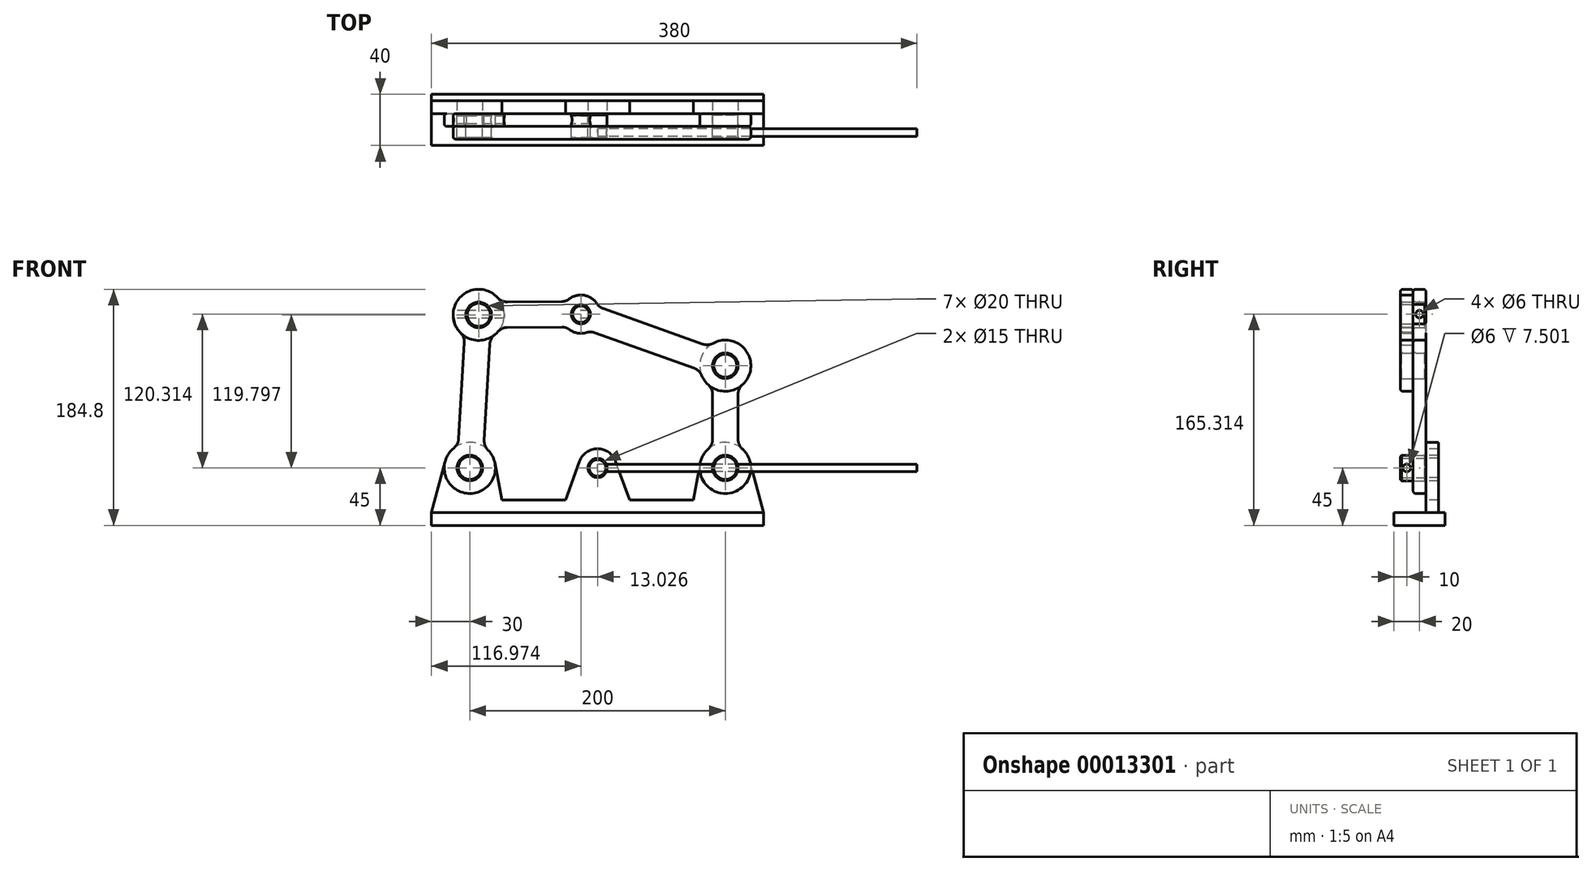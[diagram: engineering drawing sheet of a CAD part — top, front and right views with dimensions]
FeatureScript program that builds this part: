
annotation { "Feature Type Name" : "Feature", "Feature Type Description" : "" }
export const myFeature = defineFeature(function(context is Context, id is Id, definition is map)
    precondition{}
    {
        {
            var Q0;
            Q0=qCreatedBy(makeId("Front.planeOp"),FACE);
            var sketch = newSketch(context, id + "F0", { "sketchPlane" : qUnion([Q0])});
            skCircle(sketch, "E0", {"center": v(-93.03, 119.8) * mm, "radius": 20 * mm});
            skCircle(sketch, "E1", {"center": v(-93.03, 119.8) * mm, "radius": 10 * mm});
            skCircle(sketch, "E2", {"center": v(100, 80) * mm, "radius": 10 * mm});
            skCircle(sketch, "E3", {"center": v(100, 80) * mm, "radius": 20 * mm});
            skCircle(sketch, "E4", {"center": v(100, 0) * mm, "radius": 10 * mm});
            skCircle(sketch, "E5", {"center": v(100, 0) * mm, "radius": 20 * mm});
            skCircle(sketch, "E6", {"center": v(-100, 0) * mm, "radius": 10 * mm});
            skCircle(sketch, "E7", {"center": v(-100, 0) * mm, "radius": 20 * mm});
            skCircle(sketch, "E8", {"center": v(-13.03, 120.31) * mm, "radius": 7.5 * mm});
            skCircle(sketch, "E9", {"center": v(-13.03, 120.31) * mm, "radius": 15 * mm});
            skLineSegment(sketch, "E10", {"start": v(-75.77, 129.9) * mm, "end": v(-24.27, 130.24) * mm});
            skLineSegment(sketch, "E11", {"start": v(-75.64, 109.9) * mm, "end": v(-24.14, 110.24) * mm});
            skLineSegment(sketch, "E12", {"start": v(-5.85, 107.14) * mm, "end": v(80.33, 76.4) * mm});
            skLineSegment(sketch, "E13", {"start": v(90, 62.68) * mm, "end": v(90, 17.32) * mm});
            skLineSegment(sketch, "E14", {"start": v(110, 62.68) * mm, "end": v(110, 17.32) * mm});
            skLineSegment(sketch, "E15", {"start": v(-104.02, 103.09) * mm, "end": v(-108.98, 17.87) * mm});
            skLineSegment(sketch, "E16", {"start": v(-84.05, 101.92) * mm, "end": v(-89.01, 16.71) * mm});
            skLineSegment(sketch, "E17", {"start": v(0.86, 125.98) * mm, "end": v(87.05, 95.24) * mm});
            skLineSegment(sketch, "E18", {"start": v(-100, 0) * mm, "end": v(-93.03, 119.8) * mm, "construction": true});
            skLineSegment(sketch, "E19", {"start": v(-13.03, 120.31) * mm, "end": v(-93.03, 119.8) * mm, "construction": true});
            skLineSegment(sketch, "E20", {"start": v(100, 80) * mm, "end": v(-13.03, 120.31) * mm, "construction": true});
            skLineSegment(sketch, "E21", {"start": v(100, 0) * mm, "end": v(100, 80) * mm, "construction": true});
            skLineSegment(sketch, "E22", {"start": v(-100, 0) * mm, "end": v(100, 0) * mm, "construction": true});
            skLineSegment(sketch, "E23", {"start": v(-119.33, 5.14) * mm, "end": v(-130, -35) * mm});
            skLineSegment(sketch, "E24", {"start": v(-130, -35) * mm, "end": v(130, -35) * mm});
            skLineSegment(sketch, "E25", {"start": v(130, -35) * mm, "end": v(119.33, 5.14) * mm});
            skLineSegment(sketch, "E26", {"start": v(80.34, 3.66) * mm, "end": v(75, -25) * mm});
            skLineSegment(sketch, "E27", {"start": v(75, -25) * mm, "end": v(25, -25) * mm});
            skLineSegment(sketch, "E28", {"start": v(-75, -25) * mm, "end": v(-80.34, 3.66) * mm});
            skLineSegment(sketch, "E29", {"start": v(-130, -35) * mm, "end": v(-130, -45) * mm});
            skLineSegment(sketch, "E30", {"start": v(-130, -45) * mm, "end": v(130, -45) * mm});
            skLineSegment(sketch, "E31", {"start": v(130, -45) * mm, "end": v(130, -35) * mm});
            skCircle(sketch, "E32", {"center": v(0, 0) * mm, "radius": 7.5 * mm});
            skCircle(sketch, "E33", {"center": v(0, 0) * mm, "radius": 15 * mm});
            skLineSegment(sketch, "E34", {"start": v(25, -25) * mm, "end": v(14.1, 5.1) * mm});
            skLineSegment(sketch, "E35", {"start": v(-25, -25) * mm, "end": v(-14.1, 5.1) * mm});
            skLineSegment(sketch, "E36.trimOffspring", {"start": v(-25, -25) * mm, "end": v(-75, -25) * mm});
            skSolve(sketch);
        }
        {
            var Q0;
            Q0=makeQuery(id+"F0.imprint","IMPRINT",FACE,{"disambiguationData":[TD([[makeQuery(id+"F0.imprint","IMPRINT",EDGE,{"derivedFrom":sQuery(id+"F0.wireOp",EDGE,"E4")}),-1.0]])]});
            var Q1;
            {var subQ1=sQuery(id+"F0.wireOp",EDGE,"E13");Q1=makeQuery(id+"F0.imprint","IMPRINT",FACE,{"disambiguationData":[TD([[makeQuery(id+"F0.imprint","IMPRINT",EDGE,{"derivedFrom":subQ1}),1.0]])]});}
            var Q2;
            Q2=makeQuery(id+"F0.imprint","IMPRINT",FACE,{"disambiguationData":[TD([[makeQuery(id+"F0.imprint","IMPRINT",EDGE,{"derivedFrom":sQuery(id+"F0.wireOp",EDGE,"E2")}),-1.0]])]});
            extrude(context, id + "F1", {"entities" : qUnion([Q0, Q1, Q2]), "depth" : 10 * mm});
        }
        {
            var Q0;
            Q0=makeQuery(id+"F0.imprint","IMPRINT",FACE,{"disambiguationData":[TD([[makeQuery(id+"F0.imprint","IMPRINT",EDGE,{"derivedFrom":sQuery(id+"F0.wireOp",EDGE,"E2")}),-1.0]])]});
            var Q1;
            {var subQ1=sQuery(id+"F0.wireOp",EDGE,"E12");Q1=makeQuery(id+"F0.imprint","IMPRINT",FACE,{"disambiguationData":[TD([[makeQuery(id+"F0.imprint","IMPRINT",EDGE,{"derivedFrom":subQ1}),1.0]])]});}
            var Q2;
            Q2=makeQuery(id+"F0.imprint","IMPRINT",FACE,{"disambiguationData":[TD([[makeQuery(id+"F0.imprint","IMPRINT",EDGE,{"derivedFrom":sQuery(id+"F0.wireOp",EDGE,"E8")}),-1.0]])]});
            var Q3;
            {var subQ1=sQuery(id+"F0.wireOp",EDGE,"E10");Q3=makeQuery(id+"F0.imprint","IMPRINT",FACE,{"disambiguationData":[TD([[makeQuery(id+"F0.imprint","IMPRINT",EDGE,{"derivedFrom":subQ1}),-1.0]])]});}
            var Q4;
            Q4=makeQuery(id+"F0.imprint","IMPRINT",FACE,{"disambiguationData":[TD([[makeQuery(id+"F0.imprint","IMPRINT",EDGE,{"derivedFrom":sQuery(id+"F0.wireOp",EDGE,"E1")}),-1.0]])]});
            extrude(context, id + "F2", {"entities" : qUnion([Q0, Q1, Q2, Q3, Q4]), "depth" : 20 * mm, "hasSecondDirection" : true, "secondDirectionOppositeDirection" : false, "secondDirectionDepth" : 10 * mm});
        }
        {
            var Q0;
            Q0=makeQuery(id+"F0.imprint","IMPRINT",FACE,{"disambiguationData":[TD([[makeQuery(id+"F0.imprint","IMPRINT",EDGE,{"derivedFrom":sQuery(id+"F0.wireOp",EDGE,"E1")}),-1.0]])]});
            var Q1;
            {var subQ1=sQuery(id+"F0.wireOp",EDGE,"E15");Q1=makeQuery(id+"F0.imprint","IMPRINT",FACE,{"disambiguationData":[TD([[makeQuery(id+"F0.imprint","IMPRINT",EDGE,{"derivedFrom":subQ1}),1.0]])]});}
            var Q2;
            Q2=makeQuery(id+"F0.imprint","IMPRINT",FACE,{"disambiguationData":[TD([[makeQuery(id+"F0.imprint","IMPRINT",EDGE,{"derivedFrom":sQuery(id+"F0.wireOp",EDGE,"E6")}),-1.0]])]});
            extrude(context, id + "F3", {"entities" : qUnion([Q0, Q1, Q2]), "depth" : 10 * mm});
        }
        {
            var Q0;
            {var subQ6=sQuery(id+"F0.wireOp",EDGE,"E23");Q0=makeQuery(id+"F0.imprint","IMPRINT",FACE,{"disambiguationData":[TD([[makeQuery(id+"F0.imprint","IMPRINT",EDGE,{"derivedFrom":subQ6}),1.0]])]});}
            var Q1;
            Q1=makeQuery(id+"F0.imprint","IMPRINT",FACE,{"disambiguationData":[TD([[makeQuery(id+"F0.imprint","IMPRINT",EDGE,{"derivedFrom":sQuery(id+"F0.wireOp",EDGE,"E6")}),-1.0]])]});
            var Q2;
            Q2=makeQuery(id+"F0.imprint","IMPRINT",FACE,{"disambiguationData":[TD([[makeQuery(id+"F0.imprint","IMPRINT",EDGE,{"derivedFrom":sQuery(id+"F0.wireOp",EDGE,"E32")}),-1.0]])]});
            var Q3;
            Q3=makeQuery(id+"F0.imprint","IMPRINT",FACE,{"disambiguationData":[TD([[makeQuery(id+"F0.imprint","IMPRINT",EDGE,{"derivedFrom":sQuery(id+"F0.wireOp",EDGE,"E4")}),-1.0]])]});
            extrude(context, id + "F4", {"entities" : qUnion([Q0, Q1, Q2, Q3]), "oppositeDirection" : true, "depth" : 10 * mm});
        }
        {
            var Q0;
            Q0=makeQuery(id+"F0.imprint","IMPRINT",FACE,{"disambiguationData":[TD([[makeQuery(id+"F0.imprint","IMPRINT",EDGE,{"derivedFrom":sQuery(id+"F0.wireOp",EDGE,"E24")}),-1.0]])]});
            extrude(context, id + "F5", {"entities" : qUnion([Q0]), "operationType" : NewBodyOperationType.ADD, "depth" : 25 * mm, "hasSecondDirection" : true, "secondDirectionOppositeDirection" : true, "secondDirectionDepth" : 15 * mm});
        }
        {
            var Q0;
            Q0=makeQuery(id+"F0.imprint","IMPRINT",FACE,{"disambiguationData":[TD([[makeQuery(id+"F0.imprint","IMPRINT",EDGE,{"derivedFrom":sQuery(id+"F0.wireOp",EDGE,"E6")}),1.0]])]});
            var Q1;
            Q1=makeQuery(id+"F0.imprint","IMPRINT",FACE,{"disambiguationData":[TD([[makeQuery(id+"F0.imprint","IMPRINT",EDGE,{"derivedFrom":sQuery(id+"F0.wireOp",EDGE,"E1")}),1.0]])]});
            var Q2;
            Q2=makeQuery(id+"F0.imprint","IMPRINT",FACE,{"disambiguationData":[TD([[makeQuery(id+"F0.imprint","IMPRINT",EDGE,{"derivedFrom":sQuery(id+"F0.wireOp",EDGE,"E4")}),1.0]])]});
            var Q3;
            Q3=makeQuery(id+"F0.imprint","IMPRINT",FACE,{"disambiguationData":[TD([[makeQuery(id+"F0.imprint","IMPRINT",EDGE,{"derivedFrom":sQuery(id+"F0.wireOp",EDGE,"E2")}),1.0]])]});
            var Q4;
            Q4=makeQuery(id+"F0.imprint","IMPRINT",FACE,{"disambiguationData":[TD([[makeQuery(id+"F0.imprint","IMPRINT",EDGE,{"derivedFrom":sQuery(id+"F0.wireOp",EDGE,"E8")}),1.0]])]});
            var Q5;
            Q5=makeQuery(id+"F0.imprint","IMPRINT",FACE,{"disambiguationData":[TD([[makeQuery(id+"F0.imprint","IMPRINT",EDGE,{"derivedFrom":sQuery(id+"F0.wireOp",EDGE,"E32")}),1.0]])]});
            extrude(context, id + "F6", {"entities" : qUnion([Q0, Q1, Q2, Q3, Q4, Q5]), "depth" : 20 * mm});
        }
        {
            var Q0;
            Q0=qCreatedBy(makeId("Right.planeOp"),FACE);
            var sketch = newSketch(context, id + "F7", { "sketchPlane" : qUnion([Q0])});
            skCircle(sketch, "E37", {"center": v(-5, 120.31) * mm, "radius": 3 * mm});
            skCircle(sketch, "E38", {"center": v(-15, 0) * mm, "radius": 3 * mm});
            skLineSegment(sketch, "E39.0", {"start": v(-20, -7.5) * mm, "end": v(-20, 7.5) * mm, "construction": true});
            skLineSegment(sketch, "E40", {"start": v(-20, 0) * mm, "end": v(-15, 0) * mm, "construction": true});
            skLineSegment(sketch, "E41.0.0", {"start": v(0, 127.81) * mm, "end": v(0, 112.81) * mm, "construction": true});
            skLineSegment(sketch, "E42", {"start": v(0, 120.31) * mm, "end": v(-5, 120.31) * mm, "construction": true});
            skSolve(sketch);
        }
        {
            var Q0;
            Q0=makeQuery(id+"F7.imprint","IMPRINT",FACE,{"disambiguationData":[TD([[makeQuery(id+"F7.imprint","IMPRINT",EDGE,{"derivedFrom":sQuery(id+"F7.wireOp",EDGE,"E37")}),1.0]])]});
            extrude(context, id + "F8", {"entities" : qUnion([Q0]), "operationType" : NewBodyOperationType.REMOVE, "endBound" : BoundingType.THROUGH_ALL, "depth" : 25 * mm, "hasSecondDirection" : true, "secondDirectionBound" : SecondDirectionBoundingType.THROUGH_ALL, "secondDirectionOppositeDirection" : true, "secondDirectionDepth" : 25 * mm});
        }
        {
            var Q0;
            Q0=makeQuery(id+"F7.imprint","IMPRINT",FACE,{"disambiguationData":[TD([[makeQuery(id+"F7.imprint","IMPRINT",EDGE,{"derivedFrom":sQuery(id+"F7.wireOp",EDGE,"E38")}),1.0]])]});
            extrude(context, id + "F9", {"entities" : qUnion([Q0]), "operationType" : NewBodyOperationType.REMOVE, "depth" : 25 * mm});
        }
        {
            var Q0;
            Q0=makeQuery(id+"F9.boolean.opBoolean","COPY",FACE,{"derivedFrom":makeQuery(id+"F9.opExtrude","CAP_FACE",FACE,{"disambiguationData":[OSD([sQuery(id+"F7.wireOp",EDGE,"E38")])],"isStart":true})});
            extrude(context, id + "F10", {"entities" : qUnion([Q0]), "depth" : 250 * mm});
        }
        {
            var Q0;
            Q0=makeQuery(id+"F2.opExtrude","SWEPT_EDGE",EDGE,{"disambiguationData":[OSD([sQuery(id+"F0.wireOp",EDGE,"E0"),sQuery(id+"F0.wireOp",EDGE,"E10")])]});
            var Q1;
            Q1=makeQuery(id+"F2.opExtrude","SWEPT_EDGE",EDGE,{"disambiguationData":[OSD([sQuery(id+"F0.wireOp",EDGE,"E9"),sQuery(id+"F0.wireOp",EDGE,"E10")])]});
            var Q2;
            Q2=makeQuery(id+"F2.opExtrude","SWEPT_EDGE",EDGE,{"disambiguationData":[OSD([sQuery(id+"F0.wireOp",EDGE,"E9"),sQuery(id+"F0.wireOp",EDGE,"E17")])]});
            var Q3;
            Q3=makeQuery(id+"F2.opExtrude","SWEPT_EDGE",EDGE,{"disambiguationData":[OSD([sQuery(id+"F0.wireOp",EDGE,"E3"),sQuery(id+"F0.wireOp",EDGE,"E17")])]});
            var Q4;
            Q4=makeQuery(id+"F2.opExtrude","SWEPT_EDGE",EDGE,{"disambiguationData":[OSD([sQuery(id+"F0.wireOp",EDGE,"E0"),sQuery(id+"F0.wireOp",EDGE,"E11")])]});
            var Q5;
            Q5=makeQuery(id+"F3.opExtrude","SWEPT_EDGE",EDGE,{"disambiguationData":[OSD([sQuery(id+"F0.wireOp",EDGE,"E0"),sQuery(id+"F0.wireOp",EDGE,"E16")])]});
            var Q6;
            Q6=makeQuery(id+"F2.opExtrude","SWEPT_EDGE",EDGE,{"disambiguationData":[OSD([sQuery(id+"F0.wireOp",EDGE,"E9"),sQuery(id+"F0.wireOp",EDGE,"E11")])]});
            var Q7;
            Q7=makeQuery(id+"F2.opExtrude","SWEPT_EDGE",EDGE,{"disambiguationData":[OSD([sQuery(id+"F0.wireOp",EDGE,"E9"),sQuery(id+"F0.wireOp",EDGE,"E12")])]});
            var Q8;
            Q8=makeQuery(id+"F1.opExtrude","SWEPT_EDGE",EDGE,{"disambiguationData":[OSD([sQuery(id+"F0.wireOp",EDGE,"E3"),sQuery(id+"F0.wireOp",EDGE,"E13")])]});
            var Q9;
            Q9=makeQuery(id+"F2.opExtrude","SWEPT_EDGE",EDGE,{"disambiguationData":[OSD([sQuery(id+"F0.wireOp",EDGE,"E3"),sQuery(id+"F0.wireOp",EDGE,"E12")])]});
            var Q10;
            Q10=makeQuery(id+"F1.opExtrude","SWEPT_EDGE",EDGE,{"disambiguationData":[OSD([sQuery(id+"F0.wireOp",EDGE,"E5"),sQuery(id+"F0.wireOp",EDGE,"E13")])]});
            var Q11;
            Q11=makeQuery(id+"F3.opExtrude","SWEPT_EDGE",EDGE,{"disambiguationData":[OSD([sQuery(id+"F0.wireOp",EDGE,"E7"),sQuery(id+"F0.wireOp",EDGE,"E16")])]});
            var Q12;
            Q12=makeQuery(id+"F3.opExtrude","SWEPT_EDGE",EDGE,{"disambiguationData":[OSD([sQuery(id+"F0.wireOp",EDGE,"E7"),sQuery(id+"F0.wireOp",EDGE,"E15")])]});
            var Q13;
            Q13=makeQuery(id+"F3.opExtrude","SWEPT_EDGE",EDGE,{"disambiguationData":[OSD([sQuery(id+"F0.wireOp",EDGE,"E0"),sQuery(id+"F0.wireOp",EDGE,"E15")])]});
            var Q14;
            Q14=makeQuery(id+"F1.opExtrude","SWEPT_EDGE",EDGE,{"disambiguationData":[OSD([sQuery(id+"F0.wireOp",EDGE,"E5"),sQuery(id+"F0.wireOp",EDGE,"E14")])]});
            var Q15;
            Q15=makeQuery(id+"F1.opExtrude","SWEPT_EDGE",EDGE,{"disambiguationData":[OSD([sQuery(id+"F0.wireOp",EDGE,"E3"),sQuery(id+"F0.wireOp",EDGE,"E14")])]});
            fillet(context, id + "F11", {"entities" : qUnion([Q0, Q1, Q2, Q3, Q4, Q5, Q6, Q7, Q8, Q9, Q10, Q11, Q12, Q13, Q14, Q15]), "radius" : 10 * mm, "tangentPropagation" : true, "allowEdgeOverflow" : false});
        }
        {
            var Q0;
            Q0=makeQuery(id+"F3.opExtrude","CAP_FACE",FACE,{"disambiguationData":[OSD([sQuery(id+"F0.wireOp",EDGE,"E0"),sQuery(id+"F0.wireOp",EDGE,"E1"),sQuery(id+"F0.wireOp",EDGE,"E6"),sQuery(id+"F0.wireOp",EDGE,"E7"),sQuery(id+"F0.wireOp",EDGE,"E15"),sQuery(id+"F0.wireOp",EDGE,"E16")])],"isStart":false});
            var Q1;
            Q1=makeQuery(id+"F2.opExtrude","CAP_FACE",FACE,{"disambiguationData":[OSD([sQuery(id+"F0.wireOp",EDGE,"E0"),sQuery(id+"F0.wireOp",EDGE,"E1"),sQuery(id+"F0.wireOp",EDGE,"E2"),sQuery(id+"F0.wireOp",EDGE,"E3"),sQuery(id+"F0.wireOp",EDGE,"E8"),sQuery(id+"F0.wireOp",EDGE,"E9"),sQuery(id+"F0.wireOp",EDGE,"E10"),sQuery(id+"F0.wireOp",EDGE,"E11"),sQuery(id+"F0.wireOp",EDGE,"E12"),sQuery(id+"F0.wireOp",EDGE,"E17")])],"isStart":false});
            var Q2;
            Q2=makeQuery(id+"F1.opExtrude","CAP_FACE",FACE,{"disambiguationData":[OSD([sQuery(id+"F0.wireOp",EDGE,"E2"),sQuery(id+"F0.wireOp",EDGE,"E3"),sQuery(id+"F0.wireOp",EDGE,"E4"),sQuery(id+"F0.wireOp",EDGE,"E5"),sQuery(id+"F0.wireOp",EDGE,"E13"),sQuery(id+"F0.wireOp",EDGE,"E14")])],"isStart":false});
            var Q3;
            Q3=makeQuery(id+"F1.opExtrude","CAP_FACE",FACE,{"disambiguationData":[OSD([sQuery(id+"F0.wireOp",EDGE,"E2"),sQuery(id+"F0.wireOp",EDGE,"E3"),sQuery(id+"F0.wireOp",EDGE,"E4"),sQuery(id+"F0.wireOp",EDGE,"E5"),sQuery(id+"F0.wireOp",EDGE,"E13"),sQuery(id+"F0.wireOp",EDGE,"E14")])],"isStart":true});
            var Q4;
            Q4=makeQuery(id+"F2.opExtrude","CAP_FACE",FACE,{"disambiguationData":[OSD([sQuery(id+"F0.wireOp",EDGE,"E0"),sQuery(id+"F0.wireOp",EDGE,"E1"),sQuery(id+"F0.wireOp",EDGE,"E2"),sQuery(id+"F0.wireOp",EDGE,"E3"),sQuery(id+"F0.wireOp",EDGE,"E8"),sQuery(id+"F0.wireOp",EDGE,"E9"),sQuery(id+"F0.wireOp",EDGE,"E10"),sQuery(id+"F0.wireOp",EDGE,"E11"),sQuery(id+"F0.wireOp",EDGE,"E12"),sQuery(id+"F0.wireOp",EDGE,"E17")])],"isStart":true});
            var Q5;
            Q5=makeQuery(id+"F3.opExtrude","CAP_FACE",FACE,{"disambiguationData":[OSD([sQuery(id+"F0.wireOp",EDGE,"E0"),sQuery(id+"F0.wireOp",EDGE,"E1"),sQuery(id+"F0.wireOp",EDGE,"E6"),sQuery(id+"F0.wireOp",EDGE,"E7"),sQuery(id+"F0.wireOp",EDGE,"E15"),sQuery(id+"F0.wireOp",EDGE,"E16")])],"isStart":true});
            fillet(context, id + "F12", {"entities" : qUnion([Q0, Q1, Q2, Q3, Q4, Q5]), "radius" : 2 * mm, "tangentPropagation" : true, "allowEdgeOverflow" : false});
        }
        {
            var Q0;
            Q0=makeQuery(id+"F6.opExtrude","CAP_FACE",FACE,{"disambiguationData":[OSD([sQuery(id+"F0.wireOp",EDGE,"E1")])],"isStart":false});
            var Q1;
            Q1=makeQuery(id+"F6.opExtrude","CAP_FACE",FACE,{"disambiguationData":[OSD([sQuery(id+"F0.wireOp",EDGE,"E8")])],"isStart":false});
            var Q2;
            Q2=makeQuery(id+"F6.opExtrude","CAP_FACE",FACE,{"disambiguationData":[OSD([sQuery(id+"F0.wireOp",EDGE,"E6")])],"isStart":false});
            var Q3;
            Q3=makeQuery(id+"F6.opExtrude","CAP_FACE",FACE,{"disambiguationData":[OSD([sQuery(id+"F0.wireOp",EDGE,"E4")])],"isStart":false});
            var Q4;
            Q4=makeQuery(id+"F6.opExtrude","CAP_FACE",FACE,{"disambiguationData":[OSD([sQuery(id+"F0.wireOp",EDGE,"E2")])],"isStart":false});
            var Q5;
            Q5=makeQuery(id+"F6.opExtrude","CAP_FACE",FACE,{"disambiguationData":[OSD([sQuery(id+"F0.wireOp",EDGE,"E4")])],"isStart":true});
            var Q6;
            Q6=makeQuery(id+"F6.opExtrude","CAP_FACE",FACE,{"disambiguationData":[OSD([sQuery(id+"F0.wireOp",EDGE,"E2")])],"isStart":true});
            var Q7;
            Q7=makeQuery(id+"F6.opExtrude","CAP_FACE",FACE,{"disambiguationData":[OSD([sQuery(id+"F0.wireOp",EDGE,"E1")])],"isStart":true});
            var Q8;
            Q8=makeQuery(id+"F6.opExtrude","CAP_FACE",FACE,{"disambiguationData":[OSD([sQuery(id+"F0.wireOp",EDGE,"E6")])],"isStart":true});
            var Q9;
            Q9=makeQuery(id+"F6.opExtrude","CAP_FACE",FACE,{"disambiguationData":[OSD([sQuery(id+"F0.wireOp",EDGE,"E32")])],"isStart":true});
            var Q10;
            Q10=makeQuery(id+"F6.opExtrude","CAP_FACE",FACE,{"disambiguationData":[OSD([sQuery(id+"F0.wireOp",EDGE,"E32")])],"isStart":false});
            var Q11;
            Q11=makeQuery(id+"F6.opExtrude","CAP_FACE",FACE,{"disambiguationData":[OSD([sQuery(id+"F0.wireOp",EDGE,"E8")])],"isStart":true});
            chamfer(context, id + "F13", {"entities" : qUnion([Q0, Q1, Q2, Q3, Q4, Q5, Q6, Q7, Q8, Q9, Q10, Q11]), "width" : 1 * mm, "tangentPropagation" : true});
        }
    });
